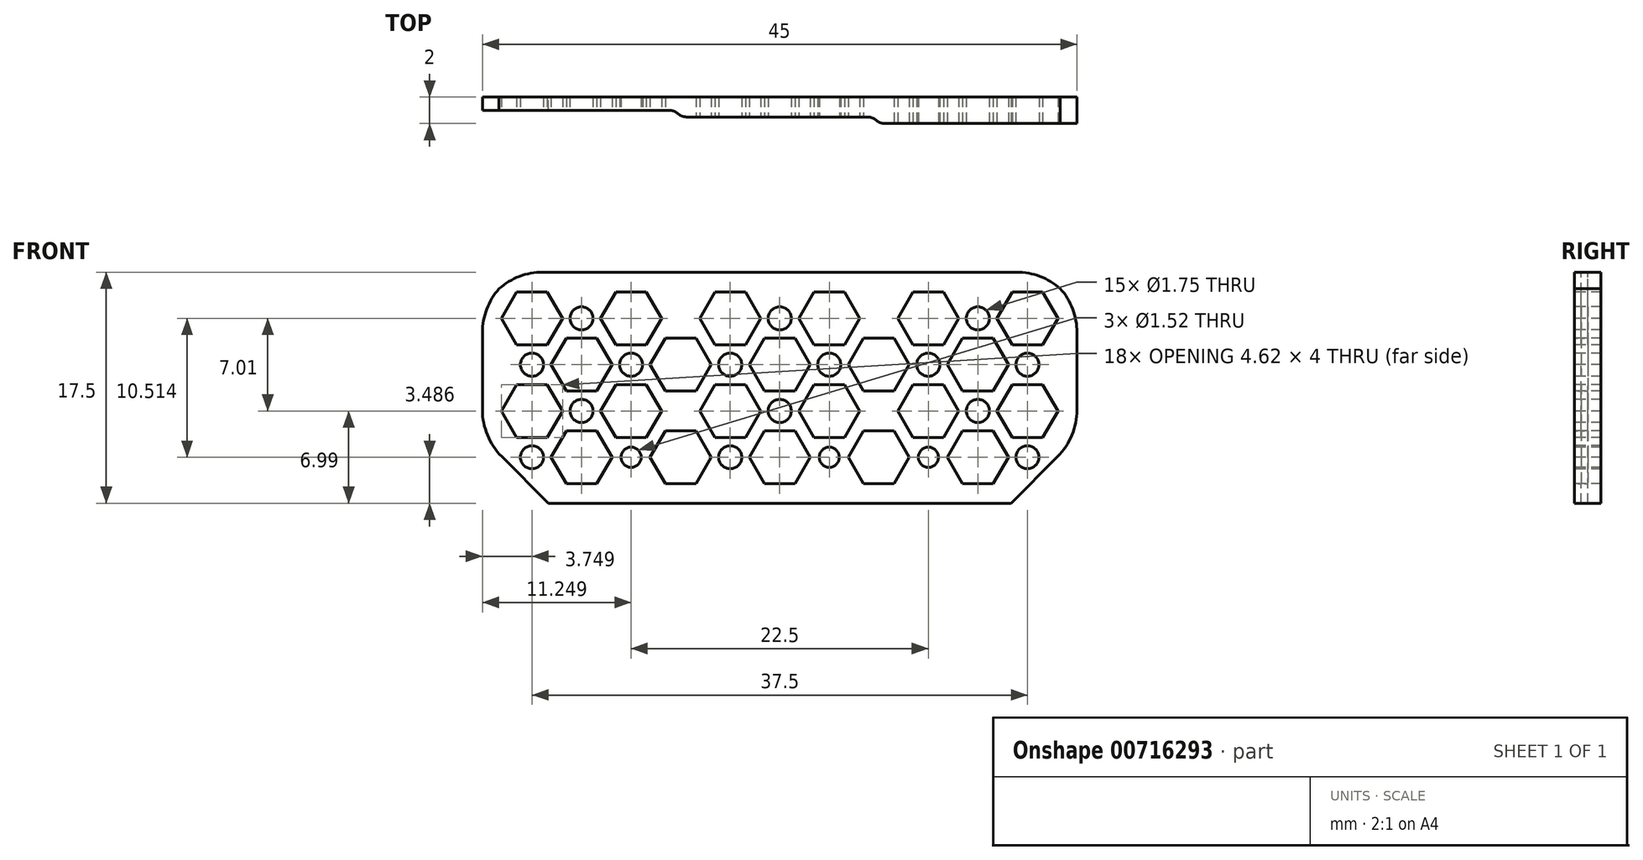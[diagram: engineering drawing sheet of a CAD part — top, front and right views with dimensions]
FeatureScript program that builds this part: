
annotation { "Feature Type Name" : "Feature", "Feature Type Description" : "" }
export const myFeature = defineFeature(function(context is Context, id is Id, definition is map)
    precondition{}
    {
        {
            var Q0;
            Q0=qCreatedBy(makeId("Top.planeOp"),FACE);
            var sketch = newSketch(context, id + "F0", { "sketchPlane" : qUnion([Q0])});
            skLineSegment(sketch, "E0.bottom", {"start": v(-22.5, 0) * mm, "end": v(-7.5, 0) * mm});
            skLineSegment(sketch, "E0.top", {"start": v(-22.5, -1) * mm, "end": v(-7.5, -1) * mm});
            skLineSegment(sketch, "E0.left", {"start": v(-22.5, 0) * mm, "end": v(-22.5, -1) * mm});
            skLineSegment(sketch, "E0.right", {"start": v(-7.5, 0) * mm, "end": v(-7.5, -1) * mm});
            skLineSegment(sketch, "E1.bottom", {"start": v(-7.5, 0) * mm, "end": v(7.5, 0) * mm});
            skLineSegment(sketch, "E1.top", {"start": v(-7.5, -1.5) * mm, "end": v(7.5, -1.5) * mm});
            skLineSegment(sketch, "E1.left", {"start": v(-7.5, 0) * mm, "end": v(-7.5, -1.5) * mm});
            skLineSegment(sketch, "E1.right", {"start": v(7.5, 0) * mm, "end": v(7.5, -1.5) * mm});
            skLineSegment(sketch, "E2.bottom", {"start": v(7.5, 0) * mm, "end": v(22.5, 0) * mm});
            skLineSegment(sketch, "E2.top", {"start": v(7.5, -2) * mm, "end": v(22.5, -2) * mm});
            skLineSegment(sketch, "E2.left", {"start": v(7.5, 0) * mm, "end": v(7.5, -2) * mm});
            skLineSegment(sketch, "E2.right", {"start": v(22.5, 0) * mm, "end": v(22.5, -2) * mm});
            skPoint(sketch, "E3", {"position": v(0, 0) * mm});
            skSolve(sketch);
        }
        {
            var Q0;
            {var subQ0=sQuery(id+"F0.wireOp",EDGE,"E0.bottom");Q0=makeQuery(id+"F0.imprint","IMPRINT",FACE,{"disambiguationData":[TD([[makeQuery(id+"F0.imprint","IMPRINT",EDGE,{"derivedFrom":subQ0}),-1.0]])]});}
            var Q1;
            {var subQ3=sQuery(id+"F0.wireOp",EDGE,"E1.bottom");Q1=makeQuery(id+"F0.imprint","IMPRINT",FACE,{"disambiguationData":[TD([[makeQuery(id+"F0.imprint","IMPRINT",EDGE,{"derivedFrom":subQ3}),-1.0]])]});}
            var Q2;
            {var subQ3=sQuery(id+"F0.wireOp",EDGE,"E2.bottom");Q2=makeQuery(id+"F0.imprint","IMPRINT",FACE,{"disambiguationData":[TD([[makeQuery(id+"F0.imprint","IMPRINT",EDGE,{"derivedFrom":subQ3}),-1.0]])]});}
            extrude(context, id + "F1", {"entities" : qUnion([Q0, Q1, Q2]), "depth" : 17.5 * mm, "offsetDistance" : 25 * mm});
        }
        {
            var Q0;
            Q0=makeQuery(id+"F1.opExtrude","SWEPT_FACE",FACE,{"disambiguationData":[OSD([sQuery(id+"F0.wireOp",EDGE,"E2.top")])]});
            var sketch = newSketch(context, id + "F2", { "sketchPlane" : qUnion([Q0])});
            skLineSegment(sketch, "E4.0.0", {"start": v(-22.5, 0) * mm, "end": v(-7.5, 0) * mm});
            skLineSegment(sketch, "E4.0.1", {"start": v(-7.5, 0) * mm, "end": v(-7.5, 17.5) * mm});
            skLineSegment(sketch, "E4.0.2", {"start": v(-7.5, 17.5) * mm, "end": v(-22.5, 17.5) * mm});
            skLineSegment(sketch, "E4.0.3", {"start": v(-22.5, 17.5) * mm, "end": v(-22.5, 0) * mm});
            skLineSegment(sketch, "E5.0.0", {"start": v(-7.5, 0) * mm, "end": v(7.5, 0) * mm});
            skLineSegment(sketch, "E5.0.1", {"start": v(7.5, 0) * mm, "end": v(7.5, 17.5) * mm});
            skLineSegment(sketch, "E5.0.2", {"start": v(7.5, 17.5) * mm, "end": v(-7.5, 17.5) * mm});
            skLineSegment(sketch, "E5.0.3", {"start": v(-7.5, 17.5) * mm, "end": v(-7.5, 0) * mm});
            skLineSegment(sketch, "E6.0.0", {"start": v(7.5, 0) * mm, "end": v(22.5, 0) * mm});
            skLineSegment(sketch, "E6.0.1", {"start": v(22.5, 0) * mm, "end": v(22.5, 17.5) * mm});
            skLineSegment(sketch, "E6.0.2", {"start": v(22.5, 17.5) * mm, "end": v(7.5, 17.5) * mm});
            skLineSegment(sketch, "E6.0.3", {"start": v(7.5, 17.5) * mm, "end": v(7.5, 0) * mm});
            skCircle(sketch, "E7.cCircle", {"center": v(18.75, 14) * mm, "radius": 2 * mm, "construction": true});
            skLineSegment(sketch, "E7.0", {"start": v(17.6, 12) * mm, "end": v(16.44, 14) * mm});
            skLineSegment(sketch, "E7.1", {"start": v(16.44, 14) * mm, "end": v(17.6, 16) * mm});
            skLineSegment(sketch, "E7.2", {"start": v(17.6, 16) * mm, "end": v(19.9, 16) * mm});
            skLineSegment(sketch, "E7.3", {"start": v(19.9, 16) * mm, "end": v(21.06, 14) * mm});
            skLineSegment(sketch, "E7.4", {"start": v(21.06, 14) * mm, "end": v(19.9, 12) * mm});
            skLineSegment(sketch, "E7.5", {"start": v(19.9, 12) * mm, "end": v(17.6, 12) * mm});
            skPoint(sketch, "E7.0.midPoint", {"position": v(17.02, 13) * mm});
            skPoint(sketch, "E8.1.0.0", {"position": v(9.52, 13) * mm});
            skLineSegment(sketch, "E8.1.0.1", {"start": v(12.4, 12) * mm, "end": v(10.1, 12) * mm});
            skLineSegment(sketch, "E8.1.0.2", {"start": v(12.4, 16) * mm, "end": v(13.56, 14) * mm});
            skCircle(sketch, "E8.1.0.3", {"center": v(11.25, 14) * mm, "radius": 2 * mm, "construction": true});
            skLineSegment(sketch, "E8.1.0.4", {"start": v(13.56, 14) * mm, "end": v(12.4, 12) * mm});
            skLineSegment(sketch, "E8.1.0.5", {"start": v(8.94, 14) * mm, "end": v(10.1, 16) * mm});
            skLineSegment(sketch, "E8.1.0.6", {"start": v(10.1, 16) * mm, "end": v(12.4, 16) * mm});
            skLineSegment(sketch, "E8.1.0.7", {"start": v(10.1, 12) * mm, "end": v(8.94, 14) * mm});
            skPoint(sketch, "E8.2.0.0", {"position": v(2.02, 13) * mm});
            skLineSegment(sketch, "E8.2.0.1", {"start": v(4.9, 12) * mm, "end": v(2.6, 12) * mm});
            skLineSegment(sketch, "E8.2.0.2", {"start": v(4.9, 16) * mm, "end": v(6.06, 14) * mm});
            skCircle(sketch, "E8.2.0.3", {"center": v(3.75, 14) * mm, "radius": 2 * mm, "construction": true});
            skLineSegment(sketch, "E8.2.0.4", {"start": v(6.06, 14) * mm, "end": v(4.9, 12) * mm});
            skLineSegment(sketch, "E8.2.0.5", {"start": v(1.44, 14) * mm, "end": v(2.6, 16) * mm});
            skLineSegment(sketch, "E8.2.0.6", {"start": v(2.6, 16) * mm, "end": v(4.9, 16) * mm});
            skLineSegment(sketch, "E8.2.0.7", {"start": v(2.6, 12) * mm, "end": v(1.44, 14) * mm});
            skLineSegment(sketch, "E8.direction1", {"start": v(17.6, 12) * mm, "end": v(10.1, 12) * mm, "construction": true});
            skPoint(sketch, "E9.0.3.0", {"position": v(-5.48, 13) * mm});
            skLineSegment(sketch, "E9.1.3.0", {"start": v(-2.6, 12) * mm, "end": v(-4.9, 12) * mm});
            skLineSegment(sketch, "E9.4.3.0", {"start": v(-2.6, 16) * mm, "end": v(-1.44, 14) * mm});
            skCircle(sketch, "E9.7.3.0", {"center": v(-3.75, 14) * mm, "radius": 2 * mm, "construction": true});
            skLineSegment(sketch, "E9.9.3.0", {"start": v(-1.44, 14) * mm, "end": v(-2.6, 12) * mm});
            skLineSegment(sketch, "E9.12.3.0", {"start": v(-6.06, 14) * mm, "end": v(-4.9, 16) * mm});
            skLineSegment(sketch, "E9.15.3.0", {"start": v(-4.9, 16) * mm, "end": v(-2.6, 16) * mm});
            skLineSegment(sketch, "E9.18.3.0", {"start": v(-4.9, 12) * mm, "end": v(-6.06, 14) * mm});
            skPoint(sketch, "E9.0.4.0", {"position": v(-12.98, 13) * mm});
            skLineSegment(sketch, "E9.1.4.0", {"start": v(-10.1, 12) * mm, "end": v(-12.4, 12) * mm});
            skLineSegment(sketch, "E9.4.4.0", {"start": v(-10.1, 16) * mm, "end": v(-8.94, 14) * mm});
            skCircle(sketch, "E9.7.4.0", {"center": v(-11.25, 14) * mm, "radius": 2 * mm, "construction": true});
            skLineSegment(sketch, "E9.9.4.0", {"start": v(-8.94, 14) * mm, "end": v(-10.1, 12) * mm});
            skLineSegment(sketch, "E9.12.4.0", {"start": v(-13.56, 14) * mm, "end": v(-12.4, 16) * mm});
            skLineSegment(sketch, "E9.15.4.0", {"start": v(-12.4, 16) * mm, "end": v(-10.1, 16) * mm});
            skLineSegment(sketch, "E9.18.4.0", {"start": v(-12.4, 12) * mm, "end": v(-13.56, 14) * mm});
            skPoint(sketch, "E9.0.5.0", {"position": v(-20.48, 13) * mm});
            skLineSegment(sketch, "E9.1.5.0", {"start": v(-17.6, 12) * mm, "end": v(-19.9, 12) * mm});
            skLineSegment(sketch, "E9.4.5.0", {"start": v(-17.6, 16) * mm, "end": v(-16.44, 14) * mm});
            skCircle(sketch, "E9.7.5.0", {"center": v(-18.75, 14) * mm, "radius": 2 * mm, "construction": true});
            skLineSegment(sketch, "E9.9.5.0", {"start": v(-16.44, 14) * mm, "end": v(-17.6, 12) * mm});
            skLineSegment(sketch, "E9.12.5.0", {"start": v(-21.06, 14) * mm, "end": v(-19.9, 16) * mm});
            skLineSegment(sketch, "E9.15.5.0", {"start": v(-19.9, 16) * mm, "end": v(-17.6, 16) * mm});
            skLineSegment(sketch, "E9.18.5.0", {"start": v(-19.9, 12) * mm, "end": v(-21.06, 14) * mm});
            skCircle(sketch, "E10.cCircle", {"center": v(15, 10.5) * mm, "radius": 2 * mm, "construction": true});
            skLineSegment(sketch, "E10.0", {"start": v(12.69, 10.5) * mm, "end": v(13.84, 12.5) * mm});
            skLineSegment(sketch, "E10.1", {"start": v(13.84, 12.5) * mm, "end": v(16.15, 12.5) * mm});
            skLineSegment(sketch, "E10.2", {"start": v(16.15, 12.5) * mm, "end": v(17.3, 10.5) * mm});
            skLineSegment(sketch, "E10.3", {"start": v(17.3, 10.5) * mm, "end": v(16.15, 8.5) * mm});
            skLineSegment(sketch, "E10.4", {"start": v(16.15, 8.5) * mm, "end": v(13.84, 8.5) * mm});
            skLineSegment(sketch, "E10.5", {"start": v(13.84, 8.5) * mm, "end": v(12.69, 10.5) * mm});
            skPoint(sketch, "E10.0.midPoint", {"position": v(13.27, 11.5) * mm});
            skLineSegment(sketch, "E11.1.0.1", {"start": v(10.1, 12) * mm, "end": v(2.6, 12) * mm, "construction": true});
            skLineSegment(sketch, "E11.1.0.2", {"start": v(6.34, 12.5) * mm, "end": v(8.65, 12.5) * mm});
            skPoint(sketch, "E11.1.0.3", {"position": v(5.77, 11.5) * mm});
            skCircle(sketch, "E11.1.0.4", {"center": v(7.5, 10.5) * mm, "radius": 2 * mm, "construction": true});
            skLineSegment(sketch, "E11.1.0.5", {"start": v(5.19, 10.5) * mm, "end": v(6.34, 12.5) * mm});
            skLineSegment(sketch, "E11.1.0.6", {"start": v(8.65, 8.5) * mm, "end": v(6.34, 8.5) * mm});
            skLineSegment(sketch, "E11.1.0.7", {"start": v(8.65, 12.5) * mm, "end": v(9.8, 10.5) * mm});
            skLineSegment(sketch, "E11.1.0.8", {"start": v(6.34, 8.5) * mm, "end": v(5.19, 10.5) * mm});
            skLineSegment(sketch, "E11.1.0.9", {"start": v(9.8, 10.5) * mm, "end": v(8.65, 8.5) * mm});
            skLineSegment(sketch, "E11.2.0.1", {"start": v(2.6, 12) * mm, "end": v(-4.9, 12) * mm, "construction": true});
            skLineSegment(sketch, "E11.2.0.2", {"start": v(-1.16, 12.5) * mm, "end": v(1.15, 12.5) * mm});
            skPoint(sketch, "E11.2.0.3", {"position": v(-1.73, 11.5) * mm});
            skCircle(sketch, "E11.2.0.4", {"center": v(0, 10.5) * mm, "radius": 2 * mm, "construction": true});
            skLineSegment(sketch, "E11.2.0.5", {"start": v(-2.31, 10.5) * mm, "end": v(-1.16, 12.5) * mm});
            skLineSegment(sketch, "E11.2.0.6", {"start": v(1.15, 8.5) * mm, "end": v(-1.16, 8.5) * mm});
            skLineSegment(sketch, "E11.2.0.7", {"start": v(1.15, 12.5) * mm, "end": v(2.3, 10.5) * mm});
            skLineSegment(sketch, "E11.2.0.8", {"start": v(-1.16, 8.5) * mm, "end": v(-2.31, 10.5) * mm});
            skLineSegment(sketch, "E11.2.0.9", {"start": v(2.3, 10.5) * mm, "end": v(1.15, 8.5) * mm});
            skLineSegment(sketch, "E11.3.0.1", {"start": v(-4.9, 12) * mm, "end": v(-12.4, 12) * mm, "construction": true});
            skLineSegment(sketch, "E11.3.0.2", {"start": v(-8.66, 12.5) * mm, "end": v(-6.35, 12.5) * mm});
            skPoint(sketch, "E11.3.0.3", {"position": v(-9.23, 11.5) * mm});
            skCircle(sketch, "E11.3.0.4", {"center": v(-7.5, 10.5) * mm, "radius": 2 * mm, "construction": true});
            skLineSegment(sketch, "E11.3.0.5", {"start": v(-9.81, 10.5) * mm, "end": v(-8.66, 12.5) * mm});
            skLineSegment(sketch, "E11.3.0.6", {"start": v(-6.35, 8.5) * mm, "end": v(-8.66, 8.5) * mm});
            skLineSegment(sketch, "E11.3.0.7", {"start": v(-6.35, 12.5) * mm, "end": v(-5.2, 10.5) * mm});
            skLineSegment(sketch, "E11.3.0.8", {"start": v(-8.66, 8.5) * mm, "end": v(-9.8, 10.5) * mm});
            skLineSegment(sketch, "E11.3.0.9", {"start": v(-5.2, 10.5) * mm, "end": v(-6.35, 8.5) * mm});
            skLineSegment(sketch, "E11.4.0.1", {"start": v(-12.4, 12) * mm, "end": v(-19.9, 12) * mm, "construction": true});
            skLineSegment(sketch, "E11.4.0.2", {"start": v(-16.16, 12.5) * mm, "end": v(-13.85, 12.5) * mm});
            skPoint(sketch, "E11.4.0.3", {"position": v(-16.73, 11.5) * mm});
            skCircle(sketch, "E11.4.0.4", {"center": v(-15, 10.5) * mm, "radius": 2 * mm, "construction": true});
            skLineSegment(sketch, "E11.4.0.5", {"start": v(-17.31, 10.5) * mm, "end": v(-16.16, 12.5) * mm});
            skLineSegment(sketch, "E11.4.0.6", {"start": v(-13.85, 8.5) * mm, "end": v(-16.16, 8.5) * mm});
            skLineSegment(sketch, "E11.4.0.7", {"start": v(-13.85, 12.5) * mm, "end": v(-12.7, 10.5) * mm});
            skLineSegment(sketch, "E11.4.0.8", {"start": v(-16.16, 8.5) * mm, "end": v(-17.3, 10.5) * mm});
            skLineSegment(sketch, "E11.4.0.9", {"start": v(-12.7, 10.5) * mm, "end": v(-13.85, 8.5) * mm});
            skLineSegment(sketch, "E11.direction1", {"start": v(10.1, 12) * mm, "end": v(2.6, 12) * mm, "construction": true});
            skPoint(sketch, "E12.1.0.0", {"position": v(-5.48, 6) * mm});
            skLineSegment(sketch, "E12.1.0.1", {"start": v(2.6, 9) * mm, "end": v(4.9, 9) * mm});
            skPoint(sketch, "E12.1.0.2", {"position": v(-20.48, 6) * mm});
            skLineSegment(sketch, "E12.1.0.3", {"start": v(-12.4, 9) * mm, "end": v(-10.1, 9) * mm});
            skLineSegment(sketch, "E12.1.0.4", {"start": v(-17.6, 9) * mm, "end": v(-16.44, 7) * mm});
            skPoint(sketch, "E12.1.0.5", {"position": v(9.52, 6) * mm});
            skPoint(sketch, "E12.1.0.6", {"position": v(2.02, 6) * mm});
            skPoint(sketch, "E12.1.0.7", {"position": v(17.02, 6) * mm});
            skLineSegment(sketch, "E12.1.0.8", {"start": v(1.44, 7) * mm, "end": v(2.6, 9) * mm});
            skLineSegment(sketch, "E12.1.0.9", {"start": v(-10.1, 9) * mm, "end": v(-8.94, 7) * mm});
            skLineSegment(sketch, "E12.1.0.10", {"start": v(-2.6, 9) * mm, "end": v(-1.44, 7) * mm});
            skPoint(sketch, "E12.1.0.11", {"position": v(-12.98, 6) * mm});
            skLineSegment(sketch, "E12.1.0.12", {"start": v(19.9, 9) * mm, "end": v(21.06, 7) * mm});
            skLineSegment(sketch, "E12.1.0.13", {"start": v(17.6, 9) * mm, "end": v(19.9, 9) * mm});
            skLineSegment(sketch, "E12.1.0.14", {"start": v(16.44, 7) * mm, "end": v(17.6, 9) * mm});
            skLineSegment(sketch, "E12.1.0.15", {"start": v(10.1, 9) * mm, "end": v(12.4, 9) * mm});
            skLineSegment(sketch, "E12.1.0.16", {"start": v(8.94, 7) * mm, "end": v(10.1, 9) * mm});
            skLineSegment(sketch, "E12.1.0.17", {"start": v(-4.9, 9) * mm, "end": v(-2.6, 9) * mm});
            skLineSegment(sketch, "E12.1.0.18", {"start": v(-13.56, 7) * mm, "end": v(-12.4, 9) * mm});
            skLineSegment(sketch, "E12.1.0.19", {"start": v(-6.06, 7) * mm, "end": v(-4.9, 9) * mm});
            skLineSegment(sketch, "E12.1.0.20", {"start": v(-19.9, 9) * mm, "end": v(-17.6, 9) * mm});
            skLineSegment(sketch, "E12.1.0.21", {"start": v(-21.06, 7) * mm, "end": v(-19.9, 9) * mm});
            skLineSegment(sketch, "E12.1.0.22", {"start": v(12.4, 9) * mm, "end": v(13.56, 7) * mm});
            skLineSegment(sketch, "E12.1.0.23", {"start": v(4.9, 9) * mm, "end": v(6.06, 7) * mm});
            skPoint(sketch, "E12.1.0.24", {"position": v(-12.98, 6) * mm});
            skPoint(sketch, "E12.1.0.25", {"position": v(2.02, 6) * mm});
            skPoint(sketch, "E12.1.0.26", {"position": v(-5.48, 6) * mm});
            skPoint(sketch, "E12.1.0.27", {"position": v(9.52, 6) * mm});
            skLineSegment(sketch, "E12.1.0.28", {"start": v(21.06, 7) * mm, "end": v(19.9, 5) * mm});
            skCircle(sketch, "E12.1.0.29", {"center": v(18.75, 7) * mm, "radius": 2 * mm, "construction": true});
            skLineSegment(sketch, "E12.1.0.30", {"start": v(17.6, 5) * mm, "end": v(16.44, 7) * mm});
            skLineSegment(sketch, "E12.1.0.31", {"start": v(19.9, 5) * mm, "end": v(17.6, 5) * mm});
            skLineSegment(sketch, "E12.1.0.32", {"start": v(17.6, 5) * mm, "end": v(10.1, 5) * mm, "construction": true});
            skLineSegment(sketch, "E12.1.0.33", {"start": v(10.1, 5) * mm, "end": v(8.94, 7) * mm});
            skLineSegment(sketch, "E12.1.0.34", {"start": v(10.1, 5) * mm, "end": v(2.6, 5) * mm, "construction": true});
            skLineSegment(sketch, "E12.1.0.35", {"start": v(13.56, 7) * mm, "end": v(12.4, 5) * mm});
            skCircle(sketch, "E12.1.0.36", {"center": v(11.25, 7) * mm, "radius": 2 * mm, "construction": true});
            skLineSegment(sketch, "E12.1.0.37", {"start": v(10.1, 5) * mm, "end": v(2.6, 5) * mm, "construction": true});
            skLineSegment(sketch, "E12.1.0.38", {"start": v(12.4, 5) * mm, "end": v(10.1, 5) * mm});
            skCircle(sketch, "E12.1.0.39", {"center": v(3.75, 7) * mm, "radius": 2 * mm, "construction": true});
            skLineSegment(sketch, "E12.1.0.40", {"start": v(4.9, 5) * mm, "end": v(2.6, 5) * mm});
            skLineSegment(sketch, "E12.1.0.41", {"start": v(2.6, 5) * mm, "end": v(1.44, 7) * mm});
            skLineSegment(sketch, "E12.1.0.42", {"start": v(2.6, 5) * mm, "end": v(-4.9, 5) * mm, "construction": true});
            skLineSegment(sketch, "E12.1.0.43", {"start": v(6.06, 7) * mm, "end": v(4.9, 5) * mm});
            skLineSegment(sketch, "E12.1.0.44", {"start": v(-4.9, 5) * mm, "end": v(-12.4, 5) * mm, "construction": true});
            skLineSegment(sketch, "E12.1.0.45", {"start": v(-4.9, 5) * mm, "end": v(-6.06, 7) * mm});
            skLineSegment(sketch, "E12.1.0.46", {"start": v(-1.44, 7) * mm, "end": v(-2.6, 5) * mm});
            skCircle(sketch, "E12.1.0.47", {"center": v(-3.75, 7) * mm, "radius": 2 * mm, "construction": true});
            skLineSegment(sketch, "E12.1.0.48", {"start": v(-2.6, 5) * mm, "end": v(-4.9, 5) * mm});
            skLineSegment(sketch, "E12.1.0.49", {"start": v(-12.4, 5) * mm, "end": v(-13.56, 7) * mm});
            skLineSegment(sketch, "E12.1.0.50", {"start": v(-8.94, 7) * mm, "end": v(-10.1, 5) * mm});
            skLineSegment(sketch, "E12.1.0.51", {"start": v(-12.4, 5) * mm, "end": v(-19.9, 5) * mm, "construction": true});
            skCircle(sketch, "E12.1.0.52", {"center": v(-11.25, 7) * mm, "radius": 2 * mm, "construction": true});
            skLineSegment(sketch, "E12.1.0.53", {"start": v(-10.1, 5) * mm, "end": v(-12.4, 5) * mm});
            skCircle(sketch, "E12.1.0.54", {"center": v(-18.75, 7) * mm, "radius": 2 * mm, "construction": true});
            skLineSegment(sketch, "E12.1.0.55", {"start": v(-16.44, 7) * mm, "end": v(-17.6, 5) * mm});
            skLineSegment(sketch, "E12.1.0.56", {"start": v(-19.9, 5) * mm, "end": v(-21.06, 7) * mm});
            skLineSegment(sketch, "E12.1.0.57", {"start": v(-17.6, 5) * mm, "end": v(-19.9, 5) * mm});
            skLineSegment(sketch, "E12.direction1", {"start": v(-20.48, 13) * mm, "end": v(-20.48, 6) * mm, "construction": true});
            skLineSegment(sketch, "E13.1.0.1", {"start": v(16.15, 1.49) * mm, "end": v(13.84, 1.49) * mm});
            skPoint(sketch, "E13.1.0.2", {"position": v(13.27, 4.49) * mm});
            skCircle(sketch, "E13.1.0.4", {"center": v(15, 3.49) * mm, "radius": 2 * mm, "construction": true});
            skLineSegment(sketch, "E13.1.0.5", {"start": v(13.84, 1.49) * mm, "end": v(12.69, 3.49) * mm});
            skLineSegment(sketch, "E13.1.0.6", {"start": v(17.3, 3.49) * mm, "end": v(16.15, 1.49) * mm});
            skLineSegment(sketch, "E13.1.0.7", {"start": v(16.15, 5.49) * mm, "end": v(17.3, 3.49) * mm});
            skLineSegment(sketch, "E13.1.0.8", {"start": v(13.84, 5.49) * mm, "end": v(16.15, 5.49) * mm});
            skLineSegment(sketch, "E13.1.0.9", {"start": v(12.69, 3.49) * mm, "end": v(13.84, 5.49) * mm});
            skPoint(sketch, "E13.1.0.10", {"position": v(5.77, 4.49) * mm});
            skLineSegment(sketch, "E13.1.0.11", {"start": v(9.8, 3.49) * mm, "end": v(8.65, 1.49) * mm});
            skCircle(sketch, "E13.1.0.12", {"center": v(7.5, 3.49) * mm, "radius": 2 * mm, "construction": true});
            skLineSegment(sketch, "E13.1.0.13", {"start": v(6.34, 5.49) * mm, "end": v(8.65, 5.49) * mm});
            skLineSegment(sketch, "E13.1.0.16", {"start": v(8.65, 1.49) * mm, "end": v(6.34, 1.49) * mm});
            skLineSegment(sketch, "E13.1.0.17", {"start": v(7.5, 10.5) * mm, "end": v(7.5, -7) * mm});
            skLineSegment(sketch, "E13.1.0.19", {"start": v(8.65, 5.49) * mm, "end": v(9.8, 3.49) * mm});
            skLineSegment(sketch, "E13.1.0.21", {"start": v(6.34, 1.49) * mm, "end": v(5.19, 3.49) * mm});
            skLineSegment(sketch, "E13.1.0.22", {"start": v(7.5, -7) * mm, "end": v(7.5, 10.5) * mm});
            skLineSegment(sketch, "E13.1.0.23", {"start": v(5.19, 3.49) * mm, "end": v(6.34, 5.49) * mm});
            skLineSegment(sketch, "E13.1.0.24", {"start": v(-1.16, 1.49) * mm, "end": v(-2.31, 3.49) * mm});
            skPoint(sketch, "E13.1.0.26", {"position": v(-1.73, 4.49) * mm});
            skCircle(sketch, "E13.1.0.27", {"center": v(0, 3.49) * mm, "radius": 2 * mm, "construction": true});
            skLineSegment(sketch, "E13.1.0.28", {"start": v(2.3, 3.49) * mm, "end": v(1.15, 1.49) * mm});
            skLineSegment(sketch, "E13.1.0.29", {"start": v(1.15, 1.49) * mm, "end": v(-1.16, 1.49) * mm});
            skLineSegment(sketch, "E13.1.0.30", {"start": v(-2.31, 3.49) * mm, "end": v(-1.16, 5.49) * mm});
            skLineSegment(sketch, "E13.1.0.31", {"start": v(1.15, 5.49) * mm, "end": v(2.3, 3.49) * mm});
            skLineSegment(sketch, "E13.1.0.32", {"start": v(-5.2, 3.49) * mm, "end": v(-6.35, 1.49) * mm});
            skCircle(sketch, "E13.1.0.33", {"center": v(-7.5, 3.49) * mm, "radius": 2 * mm, "construction": true});
            skPoint(sketch, "E13.1.0.35", {"position": v(-9.23, 4.49) * mm});
            skLineSegment(sketch, "E13.1.0.37", {"start": v(-8.66, 1.49) * mm, "end": v(-9.81, 3.49) * mm});
            skLineSegment(sketch, "E13.1.0.38", {"start": v(-7.5, 10.5) * mm, "end": v(-7.5, -7) * mm});
            skLineSegment(sketch, "E13.1.0.39", {"start": v(-6.35, 5.49) * mm, "end": v(-5.2, 3.49) * mm});
            skLineSegment(sketch, "E13.1.0.40", {"start": v(-8.66, 5.49) * mm, "end": v(-6.35, 5.49) * mm});
            skLineSegment(sketch, "E13.1.0.41", {"start": v(-6.35, 1.49) * mm, "end": v(-8.66, 1.49) * mm});
            skLineSegment(sketch, "E13.1.0.43", {"start": v(-7.5, -7) * mm, "end": v(-7.5, 10.5) * mm});
            skLineSegment(sketch, "E13.1.0.44", {"start": v(-9.81, 3.49) * mm, "end": v(-8.66, 5.49) * mm});
            skLineSegment(sketch, "E13.1.0.45", {"start": v(-1.16, 5.49) * mm, "end": v(1.15, 5.49) * mm});
            skLineSegment(sketch, "E13.1.0.46", {"start": v(-13.85, 1.49) * mm, "end": v(-16.16, 1.49) * mm});
            skPoint(sketch, "E13.1.0.47", {"position": v(-16.73, 4.49) * mm});
            skCircle(sketch, "E13.1.0.50", {"center": v(-15, 3.49) * mm, "radius": 2 * mm, "construction": true});
            skLineSegment(sketch, "E13.1.0.52", {"start": v(-16.16, 1.49) * mm, "end": v(-17.3, 3.49) * mm});
            skLineSegment(sketch, "E13.1.0.53", {"start": v(-17.31, 3.49) * mm, "end": v(-16.16, 5.49) * mm});
            skLineSegment(sketch, "E13.1.0.54", {"start": v(-16.16, 5.49) * mm, "end": v(-13.85, 5.49) * mm});
            skLineSegment(sketch, "E13.1.0.55", {"start": v(-12.7, 3.49) * mm, "end": v(-13.85, 1.49) * mm});
            skLineSegment(sketch, "E13.1.0.56", {"start": v(-13.85, 5.49) * mm, "end": v(-12.7, 3.49) * mm});
            skLineSegment(sketch, "E13.direction1", {"start": v(-7.5, 0) * mm, "end": v(-7.5, -7) * mm, "construction": true});
            skLineSegment(sketch, "E14", {"start": v(-18.75, 7) * mm, "end": v(18.75, 7) * mm, "construction": true});
            skLineSegment(sketch, "E15", {"start": v(-15, 10.5) * mm, "end": v(-15, 3.49) * mm, "construction": true});
            skLineSegment(sketch, "E16", {"start": v(-18.75, 14) * mm, "end": v(-11.25, 14) * mm, "construction": true});
            skLineSegment(sketch, "E17", {"start": v(-15, 10.5) * mm, "end": v(-15, 14) * mm, "construction": true});
            skLineSegment(sketch, "E18", {"start": v(-15, 14) * mm, "end": v(18.75, 14) * mm, "construction": true});
            skLineSegment(sketch, "E19", {"start": v(-11.25, 14) * mm, "end": v(-11.25, 7) * mm, "construction": true});
            skLineSegment(sketch, "E20", {"start": v(-7.5, 10.5) * mm, "end": v(-7.5, 3.49) * mm, "construction": true});
            skLineSegment(sketch, "E21", {"start": v(-15, 3.49) * mm, "end": v(15, 3.49) * mm, "construction": true});
            skLineSegment(sketch, "E22", {"start": v(15, 10.5) * mm, "end": v(-15, 10.5) * mm, "construction": true});
            skLineSegment(sketch, "E23", {"start": v(-3.75, 14) * mm, "end": v(-3.75, 7) * mm, "construction": true});
            skLineSegment(sketch, "E24", {"start": v(0, 10.5) * mm, "end": v(0, 3.49) * mm, "construction": true});
            skCircle(sketch, "E25", {"center": v(-15, 7) * mm, "radius": 0.88 * mm});
            skCircle(sketch, "E26", {"center": v(-15, 14) * mm, "radius": 0.88 * mm});
            skLineSegment(sketch, "E27", {"start": v(-11.25, 7) * mm, "end": v(-11.25, -10.08) * mm, "construction": true});
            skLineSegment(sketch, "E28", {"start": v(-3.75, 14) * mm, "end": v(-3.75, -4.1) * mm, "construction": true});
            skLineSegment(sketch, "E29", {"start": v(3.75, 14) * mm, "end": v(3.75, -3.7) * mm, "construction": true});
            skLineSegment(sketch, "E30", {"start": v(11.25, 14) * mm, "end": v(11.25, -4.55) * mm, "construction": true});
            skLineSegment(sketch, "E31", {"start": v(18.75, 14) * mm, "end": v(18.75, -4.4) * mm, "construction": true});
            skLineSegment(sketch, "E32", {"start": v(15, 3.49) * mm, "end": v(18.75, 3.49) * mm, "construction": true});
            skLineSegment(sketch, "E33", {"start": v(15, 10.5) * mm, "end": v(18.75, 10.5) * mm, "construction": true});
            skCircle(sketch, "E34", {"center": v(-7.5, 14) * mm, "radius": 0.88 * mm});
            skCircle(sketch, "E35", {"center": v(-7.5, 6.99) * mm, "radius": 0.88 * mm});
            skCircle(sketch, "E36", {"center": v(0, 7) * mm, "radius": 0.88 * mm});
            skCircle(sketch, "E37", {"center": v(0, 14) * mm, "radius": 0.88 * mm});
            skPoint(sketch, "E37.centerSnap0", {"position": v(0, 12.5) * mm});
            skCircle(sketch, "E38", {"center": v(7.5, 14) * mm, "radius": 0.88 * mm});
            skCircle(sketch, "E39", {"center": v(7.5, 7) * mm, "radius": 0.88 * mm});
            skCircle(sketch, "E40", {"center": v(15, 7) * mm, "radius": 0.88 * mm});
            skPoint(sketch, "E40.centerSnap0", {"position": v(15, 5.49) * mm});
            skCircle(sketch, "E41", {"center": v(15, 14) * mm, "radius": 0.88 * mm});
            skPoint(sketch, "E41.centerSnap0", {"position": v(15, 12.5) * mm});
            skCircle(sketch, "E42", {"center": v(18.75, 3.49) * mm, "radius": 0.88 * mm});
            skCircle(sketch, "E43", {"center": v(11.25, 3.49) * mm, "radius": 0.76 * mm});
            skCircle(sketch, "E44", {"center": v(-11.25, 3.49) * mm, "radius": 0.76 * mm});
            skCircle(sketch, "E45", {"center": v(-18.75, 3.49) * mm, "radius": 0.88 * mm});
            skPoint(sketch, "E45.centerSnap0", {"position": v(-18.75, 5) * mm});
            skCircle(sketch, "E46", {"center": v(-18.75, 10.5) * mm, "radius": 0.88 * mm});
            skPoint(sketch, "E46.centerSnap0", {"position": v(-18.75, 12) * mm});
            skCircle(sketch, "E47", {"center": v(-3.75, 3.49) * mm, "radius": 0.88 * mm});
            skCircle(sketch, "E48", {"center": v(3.75, 3.49) * mm, "radius": 0.76 * mm});
            skCircle(sketch, "E49", {"center": v(-3.75, 10.5) * mm, "radius": 0.88 * mm});
            skCircle(sketch, "E50", {"center": v(3.75, 10.5) * mm, "radius": 0.88 * mm});
            skCircle(sketch, "E51", {"center": v(11.25, 10.5) * mm, "radius": 0.88 * mm});
            skCircle(sketch, "E52", {"center": v(18.75, 10.5) * mm, "radius": 0.88 * mm});
            skCircle(sketch, "E53", {"center": v(-11.25, 10.5) * mm, "radius": 0.88 * mm});
            skSolve(sketch);
        }
        {
            var Q0;
            Q0=makeQuery(id+"F2.imprint","IMPRINT",FACE,{"disambiguationData":[TD([[makeQuery(id+"F2.imprint","IMPRINT",EDGE,{"derivedFrom":sQuery(id+"F2.wireOp",EDGE,"E9.1.5.0")}),-1.0]])]});
            var Q1;
            Q1=makeQuery(id+"F2.imprint","IMPRINT",FACE,{"disambiguationData":[TD([[makeQuery(id+"F2.imprint","IMPRINT",EDGE,{"derivedFrom":sQuery(id+"F2.wireOp",EDGE,"E46")}),1.0]])]});
            var Q2;
            Q2=makeQuery(id+"F2.imprint","IMPRINT",FACE,{"disambiguationData":[TD([[makeQuery(id+"F2.imprint","IMPRINT",EDGE,{"derivedFrom":sQuery(id+"F2.wireOp",EDGE,"E12.1.0.4")}),-1.0]])]});
            var Q3;
            Q3=makeQuery(id+"F2.imprint","IMPRINT",FACE,{"disambiguationData":[TD([[makeQuery(id+"F2.imprint","IMPRINT",EDGE,{"derivedFrom":sQuery(id+"F2.wireOp",EDGE,"E45")}),1.0]])]});
            var Q4;
            Q4=makeQuery(id+"F2.imprint","IMPRINT",FACE,{"disambiguationData":[TD([[makeQuery(id+"F2.imprint","IMPRINT",EDGE,{"derivedFrom":sQuery(id+"F2.wireOp",EDGE,"E13.1.0.46")}),-1.0]])]});
            var Q5;
            Q5=makeQuery(id+"F2.imprint","IMPRINT",FACE,{"disambiguationData":[TD([[makeQuery(id+"F2.imprint","IMPRINT",EDGE,{"derivedFrom":sQuery(id+"F2.wireOp",EDGE,"E25")}),1.0]])]});
            var Q6;
            Q6=makeQuery(id+"F2.imprint","IMPRINT",FACE,{"disambiguationData":[TD([[makeQuery(id+"F2.imprint","IMPRINT",EDGE,{"derivedFrom":sQuery(id+"F2.wireOp",EDGE,"E11.4.0.2")}),-1.0]])]});
            var Q7;
            Q7=makeQuery(id+"F2.imprint","IMPRINT",FACE,{"disambiguationData":[TD([[makeQuery(id+"F2.imprint","IMPRINT",EDGE,{"derivedFrom":sQuery(id+"F2.wireOp",EDGE,"E26")}),1.0]])]});
            var Q8;
            Q8=makeQuery(id+"F2.imprint","IMPRINT",FACE,{"disambiguationData":[TD([[makeQuery(id+"F2.imprint","IMPRINT",EDGE,{"derivedFrom":sQuery(id+"F2.wireOp",EDGE,"E9.1.4.0")}),-1.0]])]});
            var Q9;
            Q9=makeQuery(id+"F2.imprint","IMPRINT",FACE,{"disambiguationData":[TD([[makeQuery(id+"F2.imprint","IMPRINT",EDGE,{"derivedFrom":sQuery(id+"F2.wireOp",EDGE,"E12.1.0.3")}),-1.0]])]});
            var Q10;
            Q10=makeQuery(id+"F2.imprint","IMPRINT",FACE,{"disambiguationData":[TD([[makeQuery(id+"F2.imprint","IMPRINT",EDGE,{"derivedFrom":sQuery(id+"F2.wireOp",EDGE,"E44")}),1.0]])]});
            var Q11;
            {var subQ5=sQuery(id+"F2.wireOp",EDGE,"E13.1.0.32");Q11=makeQuery(id+"F2.imprint","IMPRINT",FACE,{"disambiguationData":[TD([[makeQuery(id+"F2.imprint","IMPRINT",EDGE,{"derivedFrom":subQ5}),-1.0]])]});}
            var Q12;
            {var subQ6=sQuery(id+"F2.wireOp",EDGE,"E13.1.0.37");Q12=makeQuery(id+"F2.imprint","IMPRINT",FACE,{"disambiguationData":[TD([[makeQuery(id+"F2.imprint","IMPRINT",EDGE,{"derivedFrom":subQ6}),-1.0]])]});}
            var Q13;
            {var subQ0=sQuery(id+"F2.wireOp",EDGE,"E35");var subQ1=sQuery(id+"F2.wireOp",EDGE,"E13.1.0.43");var subQ2=makeQuery(id+"F2.imprint","INTERSECT",VERTEX,{"disambiguationData":[OD(0.0)],"derivedFrom":[subQ1,subQ0]});Q13=makeQuery(id+"F2.imprint","IMPRINT",FACE,{"disambiguationData":[TD([[makeQuery(id+"F2.imprint","IMPRINT",EDGE,{"disambiguationData":[TD([[subQ2,-1.0]])],"derivedFrom":subQ1}),1.0]])]});}
            var Q14;
            {var subQ0=sQuery(id+"F2.wireOp",EDGE,"E35");var subQ1=sQuery(id+"F2.wireOp",EDGE,"E13.1.0.43");var subQ2=makeQuery(id+"F2.imprint","INTERSECT",VERTEX,{"disambiguationData":[OD(0.0)],"derivedFrom":[subQ1,subQ0]});Q14=makeQuery(id+"F2.imprint","IMPRINT",FACE,{"disambiguationData":[TD([[makeQuery(id+"F2.imprint","IMPRINT",EDGE,{"disambiguationData":[TD([[subQ2,-1.0]])],"derivedFrom":subQ1}),-1.0]])]});}
            var Q15;
            {var subQ0=sQuery(id+"F2.wireOp",EDGE,"E11.3.0.7");Q15=makeQuery(id+"F2.imprint","IMPRINT",FACE,{"disambiguationData":[TD([[makeQuery(id+"F2.imprint","IMPRINT",EDGE,{"derivedFrom":subQ0}),-1.0]])]});}
            var Q16;
            {var subQ4=sQuery(id+"F2.wireOp",EDGE,"E11.3.0.5");Q16=makeQuery(id+"F2.imprint","IMPRINT",FACE,{"disambiguationData":[TD([[makeQuery(id+"F2.imprint","IMPRINT",EDGE,{"derivedFrom":subQ4}),-1.0]])]});}
            var Q17;
            {var subQ0=sQuery(id+"F2.wireOp",EDGE,"E34");var subQ1=sQuery(id+"F2.wireOp",EDGE,"E5.0.3");var subQ2=makeQuery(id+"F2.imprint","INTERSECT",VERTEX,{"disambiguationData":[OD(0.0)],"derivedFrom":[subQ1,subQ0]});Q17=makeQuery(id+"F2.imprint","IMPRINT",FACE,{"disambiguationData":[TD([[makeQuery(id+"F2.imprint","IMPRINT",EDGE,{"disambiguationData":[TD([[subQ2,-1.0]])],"derivedFrom":subQ1}),-1.0]])]});}
            var Q18;
            {var subQ0=sQuery(id+"F2.wireOp",EDGE,"E34");var subQ1=sQuery(id+"F2.wireOp",EDGE,"E5.0.3");var subQ2=makeQuery(id+"F2.imprint","INTERSECT",VERTEX,{"disambiguationData":[OD(0.0)],"derivedFrom":[subQ1,subQ0]});Q18=makeQuery(id+"F2.imprint","IMPRINT",FACE,{"disambiguationData":[TD([[makeQuery(id+"F2.imprint","IMPRINT",EDGE,{"disambiguationData":[TD([[subQ2,-1.0]])],"derivedFrom":subQ1}),1.0]])]});}
            var Q19;
            Q19=makeQuery(id+"F2.imprint","IMPRINT",FACE,{"disambiguationData":[TD([[makeQuery(id+"F2.imprint","IMPRINT",EDGE,{"derivedFrom":sQuery(id+"F2.wireOp",EDGE,"E9.1.3.0")}),-1.0]])]});
            var Q20;
            Q20=makeQuery(id+"F2.imprint","IMPRINT",FACE,{"disambiguationData":[TD([[makeQuery(id+"F2.imprint","IMPRINT",EDGE,{"derivedFrom":sQuery(id+"F2.wireOp",EDGE,"E12.1.0.10")}),-1.0]])]});
            var Q21;
            Q21=makeQuery(id+"F2.imprint","IMPRINT",FACE,{"disambiguationData":[TD([[makeQuery(id+"F2.imprint","IMPRINT",EDGE,{"derivedFrom":sQuery(id+"F2.wireOp",EDGE,"E12.1.0.1")}),-1.0]])]});
            var Q22;
            Q22=makeQuery(id+"F2.imprint","IMPRINT",FACE,{"disambiguationData":[TD([[makeQuery(id+"F2.imprint","IMPRINT",EDGE,{"derivedFrom":sQuery(id+"F2.wireOp",EDGE,"E11.2.0.2")}),-1.0]])]});
            var Q23;
            Q23=makeQuery(id+"F2.imprint","IMPRINT",FACE,{"disambiguationData":[TD([[makeQuery(id+"F2.imprint","IMPRINT",EDGE,{"derivedFrom":sQuery(id+"F2.wireOp",EDGE,"E8.2.0.1")}),-1.0]])]});
            var Q24;
            {var subQ0=sQuery(id+"F2.wireOp",EDGE,"E11.1.0.7");Q24=makeQuery(id+"F2.imprint","IMPRINT",FACE,{"disambiguationData":[TD([[makeQuery(id+"F2.imprint","IMPRINT",EDGE,{"derivedFrom":subQ0}),-1.0]])]});}
            var Q25;
            {var subQ1=sQuery(id+"F2.wireOp",EDGE,"E13.1.0.11");Q25=makeQuery(id+"F2.imprint","IMPRINT",FACE,{"disambiguationData":[TD([[makeQuery(id+"F2.imprint","IMPRINT",EDGE,{"derivedFrom":subQ1}),-1.0]])]});}
            var Q26;
            {var subQ0=sQuery(id+"F2.wireOp",EDGE,"E13.1.0.21");Q26=makeQuery(id+"F2.imprint","IMPRINT",FACE,{"disambiguationData":[TD([[makeQuery(id+"F2.imprint","IMPRINT",EDGE,{"derivedFrom":subQ0}),-1.0]])]});}
            var Q27;
            {var subQ4=sQuery(id+"F2.wireOp",EDGE,"E11.1.0.5");Q27=makeQuery(id+"F2.imprint","IMPRINT",FACE,{"disambiguationData":[TD([[makeQuery(id+"F2.imprint","IMPRINT",EDGE,{"derivedFrom":subQ4}),-1.0]])]});}
            var Q28;
            Q28=makeQuery(id+"F2.imprint","IMPRINT",FACE,{"disambiguationData":[TD([[makeQuery(id+"F2.imprint","IMPRINT",EDGE,{"derivedFrom":sQuery(id+"F2.wireOp",EDGE,"E8.1.0.1")}),-1.0]])]});
            var Q29;
            Q29=makeQuery(id+"F2.imprint","IMPRINT",FACE,{"disambiguationData":[TD([[makeQuery(id+"F2.imprint","IMPRINT",EDGE,{"derivedFrom":sQuery(id+"F2.wireOp",EDGE,"E7.0")}),-1.0]])]});
            var Q30;
            Q30=makeQuery(id+"F2.imprint","IMPRINT",FACE,{"disambiguationData":[TD([[makeQuery(id+"F2.imprint","IMPRINT",EDGE,{"derivedFrom":sQuery(id+"F2.wireOp",EDGE,"E12.1.0.12")}),-1.0]])]});
            var Q31;
            Q31=makeQuery(id+"F2.imprint","IMPRINT",FACE,{"disambiguationData":[TD([[makeQuery(id+"F2.imprint","IMPRINT",EDGE,{"derivedFrom":sQuery(id+"F2.wireOp",EDGE,"E13.1.0.1")}),-1.0]])]});
            var Q32;
            Q32=makeQuery(id+"F2.imprint","IMPRINT",FACE,{"disambiguationData":[TD([[makeQuery(id+"F2.imprint","IMPRINT",EDGE,{"derivedFrom":sQuery(id+"F2.wireOp",EDGE,"E10.0")}),-1.0]])]});
            var Q33;
            Q33=makeQuery(id+"F2.imprint","IMPRINT",FACE,{"disambiguationData":[TD([[makeQuery(id+"F2.imprint","IMPRINT",EDGE,{"derivedFrom":sQuery(id+"F2.wireOp",EDGE,"E41")}),1.0]])]});
            var Q34;
            Q34=makeQuery(id+"F2.imprint","IMPRINT",FACE,{"disambiguationData":[TD([[makeQuery(id+"F2.imprint","IMPRINT",EDGE,{"derivedFrom":sQuery(id+"F2.wireOp",EDGE,"E40")}),1.0]])]});
            var Q35;
            Q35=makeQuery(id+"F2.imprint","IMPRINT",FACE,{"disambiguationData":[TD([[makeQuery(id+"F2.imprint","IMPRINT",EDGE,{"derivedFrom":sQuery(id+"F2.wireOp",EDGE,"E52")}),1.0]])]});
            var Q36;
            Q36=makeQuery(id+"F2.imprint","IMPRINT",FACE,{"disambiguationData":[TD([[makeQuery(id+"F2.imprint","IMPRINT",EDGE,{"derivedFrom":sQuery(id+"F2.wireOp",EDGE,"E42")}),1.0]])]});
            var Q37;
            Q37=makeQuery(id+"F2.imprint","IMPRINT",FACE,{"disambiguationData":[TD([[makeQuery(id+"F2.imprint","IMPRINT",EDGE,{"derivedFrom":sQuery(id+"F2.wireOp",EDGE,"E43")}),1.0]])]});
            var Q38;
            Q38=makeQuery(id+"F2.imprint","IMPRINT",FACE,{"disambiguationData":[TD([[makeQuery(id+"F2.imprint","IMPRINT",EDGE,{"derivedFrom":sQuery(id+"F2.wireOp",EDGE,"E12.1.0.15")}),-1.0]])]});
            var Q39;
            Q39=makeQuery(id+"F2.imprint","IMPRINT",FACE,{"disambiguationData":[TD([[makeQuery(id+"F2.imprint","IMPRINT",EDGE,{"derivedFrom":sQuery(id+"F2.wireOp",EDGE,"E51")}),1.0]])]});
            var Q40;
            {var subQ0=sQuery(id+"F2.wireOp",EDGE,"E39");var subQ1=sQuery(id+"F2.wireOp",EDGE,"E13.1.0.22");var subQ2=makeQuery(id+"F2.imprint","INTERSECT",VERTEX,{"disambiguationData":[OD(0.0)],"derivedFrom":[subQ1,subQ0]});Q40=makeQuery(id+"F2.imprint","IMPRINT",FACE,{"disambiguationData":[TD([[makeQuery(id+"F2.imprint","IMPRINT",EDGE,{"disambiguationData":[TD([[subQ2,-1.0]])],"derivedFrom":subQ1}),1.0]])]});}
            var Q41;
            {var subQ0=sQuery(id+"F2.wireOp",EDGE,"E39");var subQ1=sQuery(id+"F2.wireOp",EDGE,"E13.1.0.22");var subQ2=makeQuery(id+"F2.imprint","INTERSECT",VERTEX,{"disambiguationData":[OD(0.0)],"derivedFrom":[subQ1,subQ0]});Q41=makeQuery(id+"F2.imprint","IMPRINT",FACE,{"disambiguationData":[TD([[makeQuery(id+"F2.imprint","IMPRINT",EDGE,{"disambiguationData":[TD([[subQ2,-1.0]])],"derivedFrom":subQ1}),-1.0]])]});}
            var Q42;
            {var subQ0=sQuery(id+"F2.wireOp",EDGE,"E38");var subQ1=sQuery(id+"F2.wireOp",EDGE,"E6.0.3");var subQ2=makeQuery(id+"F2.imprint","INTERSECT",VERTEX,{"disambiguationData":[OD(0.0)],"derivedFrom":[subQ1,subQ0]});Q42=makeQuery(id+"F2.imprint","IMPRINT",FACE,{"disambiguationData":[TD([[makeQuery(id+"F2.imprint","IMPRINT",EDGE,{"disambiguationData":[TD([[subQ2,-1.0]])],"derivedFrom":subQ1}),1.0]])]});}
            var Q43;
            {var subQ0=sQuery(id+"F2.wireOp",EDGE,"E38");var subQ1=sQuery(id+"F2.wireOp",EDGE,"E6.0.3");var subQ2=makeQuery(id+"F2.imprint","INTERSECT",VERTEX,{"disambiguationData":[OD(0.0)],"derivedFrom":[subQ1,subQ0]});Q43=makeQuery(id+"F2.imprint","IMPRINT",FACE,{"disambiguationData":[TD([[makeQuery(id+"F2.imprint","IMPRINT",EDGE,{"disambiguationData":[TD([[subQ2,-1.0]])],"derivedFrom":subQ1}),-1.0]])]});}
            var Q44;
            Q44=makeQuery(id+"F2.imprint","IMPRINT",FACE,{"disambiguationData":[TD([[makeQuery(id+"F2.imprint","IMPRINT",EDGE,{"derivedFrom":sQuery(id+"F2.wireOp",EDGE,"E50")}),1.0]])]});
            var Q45;
            Q45=makeQuery(id+"F2.imprint","IMPRINT",FACE,{"disambiguationData":[TD([[makeQuery(id+"F2.imprint","IMPRINT",EDGE,{"derivedFrom":sQuery(id+"F2.wireOp",EDGE,"E36")}),1.0]])]});
            var Q46;
            Q46=makeQuery(id+"F2.imprint","IMPRINT",FACE,{"disambiguationData":[TD([[makeQuery(id+"F2.imprint","IMPRINT",EDGE,{"derivedFrom":sQuery(id+"F2.wireOp",EDGE,"E13.1.0.24")}),-1.0]])]});
            var Q47;
            Q47=makeQuery(id+"F2.imprint","IMPRINT",FACE,{"disambiguationData":[TD([[makeQuery(id+"F2.imprint","IMPRINT",EDGE,{"derivedFrom":sQuery(id+"F2.wireOp",EDGE,"E47")}),1.0]])]});
            var Q48;
            Q48=makeQuery(id+"F2.imprint","IMPRINT",FACE,{"disambiguationData":[TD([[makeQuery(id+"F2.imprint","IMPRINT",EDGE,{"derivedFrom":sQuery(id+"F2.wireOp",EDGE,"E48")}),1.0]])]});
            var Q49;
            Q49=makeQuery(id+"F2.imprint","IMPRINT",FACE,{"disambiguationData":[TD([[makeQuery(id+"F2.imprint","IMPRINT",EDGE,{"derivedFrom":sQuery(id+"F2.wireOp",EDGE,"E49")}),1.0]])]});
            var Q50;
            Q50=makeQuery(id+"F2.imprint","IMPRINT",FACE,{"disambiguationData":[TD([[makeQuery(id+"F2.imprint","IMPRINT",EDGE,{"derivedFrom":sQuery(id+"F2.wireOp",EDGE,"E37")}),1.0]])]});
            var Q51;
            Q51=makeQuery(id+"F2.imprint","IMPRINT",FACE,{"disambiguationData":[TD([[makeQuery(id+"F2.imprint","IMPRINT",EDGE,{"derivedFrom":sQuery(id+"F2.wireOp",EDGE,"E53")}),1.0]])]});
            extrude(context, id + "F3", {"entities" : qUnion([Q0, Q1, Q2, Q3, Q4, Q5, Q6, Q7, Q8, Q9, Q10, Q11, Q12, Q13, Q14, Q15, Q16, Q17, Q18, Q19, Q20, Q21, Q22, Q23, Q24, Q25, Q26, Q27, Q28, Q29, Q30, Q31, Q32, Q33, Q34, Q35, Q36, Q37, Q38, Q39, Q40, Q41, Q42, Q43, Q44, Q45, Q46, Q47, Q48, Q49, Q50, Q51]), "operationType" : NewBodyOperationType.REMOVE, "oppositeDirection" : true, "depth" : 25 * mm, "offsetDistance" : 25 * mm});
        }
        {
            var Q0;
            Q0=makeQuery(id+"F1.opExtrude","CAP_EDGE",EDGE,{"disambiguationData":[OSD([sQuery(id+"F0.wireOp",EDGE,"E0.left")])],"isStart":true});
            var Q1;
            Q1=makeQuery(id+"F1.opExtrude","CAP_EDGE",EDGE,{"disambiguationData":[OSD([sQuery(id+"F0.wireOp",EDGE,"E2.right")])],"isStart":true});
            chamfer(context, id + "F4", {"entities" : qUnion([Q0, Q1]), "width" : 5 * mm, "tangentPropagation" : true});
        }
        {
            var Q0;
            Q0=makeQuery(id+"F1.opExtrude","CAP_EDGE",EDGE,{"disambiguationData":[OSD([sQuery(id+"F0.wireOp",EDGE,"E0.left")])],"isStart":false});
            var Q1;
            Q1=makeQuery(id+"F1.opExtrude","CAP_EDGE",EDGE,{"disambiguationData":[OSD([sQuery(id+"F0.wireOp",EDGE,"E2.right")])],"isStart":false});
            chamfer(context, id + "F5", {"entities" : qUnion([Q0, Q1]), "width" : 2.5 * mm, "tangentPropagation" : true});
        }
        {
            var Q0;
            {var subQ0=sQuery(id+"F0.wireOp",EDGE,"E1.left");var subQ1=sQuery(id+"F0.wireOp",EDGE,"E0.top");Q0=makeQuery(id+"F3.boolean.opBoolean","SPLIT",EDGE,{"disambiguationData":[TD([makeQuery(id+"F1.opExtrude","CAP_FACE",FACE,{"disambiguationData":[OSD([sQuery(id+"F0.wireOp",EDGE,"E0.bottom"),subQ1,sQuery(id+"F0.wireOp",EDGE,"E0.left"),sQuery(id+"F0.wireOp",EDGE,"E1.bottom"),sQuery(id+"F0.wireOp",EDGE,"E1.top"),subQ0,sQuery(id+"F0.wireOp",EDGE,"E2.bottom"),sQuery(id+"F0.wireOp",EDGE,"E2.top"),sQuery(id+"F0.wireOp",EDGE,"E2.left"),sQuery(id+"F0.wireOp",EDGE,"E2.right")])],"isStart":false})])],"derivedFrom":makeQuery(id+"F1.opExtrude","SWEPT_EDGE",EDGE,{"disambiguationData":[OSD([subQ1,subQ0])]})});}
            var Q1;
            {var subQ0=sQuery(id+"F0.wireOp",EDGE,"E0.top");var subQ1=sQuery(id+"F0.wireOp",EDGE,"E1.left");Q1=makeQuery(id+"F3.boolean.opBoolean","SPLIT",EDGE,{"disambiguationData":[TD([makeQuery(id+"F3.opExtrude","SWEPT_FACE",FACE,{"disambiguationData":[OSD([sQuery(id+"F2.wireOp",EDGE,"E11.3.0.6")])]})])],"derivedFrom":makeQuery(id+"F1.opExtrude","SWEPT_EDGE",EDGE,{"disambiguationData":[OSD([subQ0,subQ1])]})});}
            var Q2;
            {var subQ0=sQuery(id+"F0.wireOp",EDGE,"E0.top");var subQ1=sQuery(id+"F0.wireOp",EDGE,"E1.left");Q2=makeQuery(id+"F3.boolean.opBoolean","SPLIT",EDGE,{"disambiguationData":[TD([makeQuery(id+"F3.opExtrude","SWEPT_FACE",FACE,{"disambiguationData":[OSD([sQuery(id+"F2.wireOp",EDGE,"E13.1.0.40")])]})])],"derivedFrom":makeQuery(id+"F1.opExtrude","SWEPT_EDGE",EDGE,{"disambiguationData":[OSD([subQ0,subQ1])]})});}
            var Q3;
            {var subQ0=sQuery(id+"F0.wireOp",EDGE,"E1.left");var subQ1=sQuery(id+"F0.wireOp",EDGE,"E0.top");Q3=makeQuery(id+"F3.boolean.opBoolean","SPLIT",EDGE,{"disambiguationData":[TD([makeQuery(id+"F3.opExtrude","SWEPT_FACE",FACE,{"disambiguationData":[OSD([sQuery(id+"F2.wireOp",EDGE,"E13.1.0.41")])]})])],"derivedFrom":makeQuery(id+"F1.opExtrude","SWEPT_EDGE",EDGE,{"disambiguationData":[OSD([subQ1,subQ0])]})});}
            var Q4;
            {var subQ0=sQuery(id+"F0.wireOp",EDGE,"E0.top");var subQ1=sQuery(id+"F0.wireOp",EDGE,"E1.left");Q4=makeQuery(id+"F3.boolean.opBoolean","SPLIT",EDGE,{"disambiguationData":[TD([makeQuery(id+"F3.opExtrude","SWEPT_FACE",FACE,{"disambiguationData":[OSD([sQuery(id+"F2.wireOp",EDGE,"E11.3.0.2")])]})])],"derivedFrom":makeQuery(id+"F1.opExtrude","SWEPT_EDGE",EDGE,{"disambiguationData":[OSD([subQ0,subQ1])]})});}
            fillet(context, id + "F6", {"entities" : qUnion([Q0, Q1, Q2, Q3, Q4]), "radius" : 1 * mm, "tangentPropagation" : true, "allowEdgeOverflow" : false});
        }
        {
            var Q0;
            {var subQ0=sQuery(id+"F0.wireOp",EDGE,"E2.left");var subQ1=sQuery(id+"F0.wireOp",EDGE,"E1.top");Q0=makeQuery(id+"F3.boolean.opBoolean","SPLIT",EDGE,{"disambiguationData":[TD([makeQuery(id+"F1.opExtrude","CAP_FACE",FACE,{"disambiguationData":[OSD([sQuery(id+"F0.wireOp",EDGE,"E0.bottom"),sQuery(id+"F0.wireOp",EDGE,"E0.top"),sQuery(id+"F0.wireOp",EDGE,"E0.left"),sQuery(id+"F0.wireOp",EDGE,"E1.bottom"),subQ1,sQuery(id+"F0.wireOp",EDGE,"E1.left"),sQuery(id+"F0.wireOp",EDGE,"E2.bottom"),sQuery(id+"F0.wireOp",EDGE,"E2.top"),subQ0,sQuery(id+"F0.wireOp",EDGE,"E2.right")])],"isStart":false})])],"derivedFrom":makeQuery(id+"F1.opExtrude","SWEPT_EDGE",EDGE,{"disambiguationData":[OSD([subQ1,subQ0])]})});}
            var Q1;
            {var subQ0=sQuery(id+"F0.wireOp",EDGE,"E2.left");var subQ1=sQuery(id+"F0.wireOp",EDGE,"E1.top");Q1=makeQuery(id+"F3.boolean.opBoolean","SPLIT",EDGE,{"disambiguationData":[TD([makeQuery(id+"F3.opExtrude","SWEPT_FACE",FACE,{"disambiguationData":[OSD([sQuery(id+"F2.wireOp",EDGE,"E13.1.0.16")])]})])],"derivedFrom":makeQuery(id+"F1.opExtrude","SWEPT_EDGE",EDGE,{"disambiguationData":[OSD([subQ1,subQ0])]})});}
            var Q2;
            {var subQ0=sQuery(id+"F0.wireOp",EDGE,"E1.top");var subQ1=sQuery(id+"F0.wireOp",EDGE,"E2.left");Q2=makeQuery(id+"F3.boolean.opBoolean","SPLIT",EDGE,{"disambiguationData":[TD([makeQuery(id+"F3.opExtrude","SWEPT_FACE",FACE,{"disambiguationData":[OSD([sQuery(id+"F2.wireOp",EDGE,"E13.1.0.13")])]})])],"derivedFrom":makeQuery(id+"F1.opExtrude","SWEPT_EDGE",EDGE,{"disambiguationData":[OSD([subQ0,subQ1])]})});}
            var Q3;
            {var subQ0=sQuery(id+"F0.wireOp",EDGE,"E1.top");var subQ1=sQuery(id+"F0.wireOp",EDGE,"E2.left");Q3=makeQuery(id+"F3.boolean.opBoolean","SPLIT",EDGE,{"disambiguationData":[TD([makeQuery(id+"F3.opExtrude","SWEPT_FACE",FACE,{"disambiguationData":[OSD([sQuery(id+"F2.wireOp",EDGE,"E11.1.0.6")])]})])],"derivedFrom":makeQuery(id+"F1.opExtrude","SWEPT_EDGE",EDGE,{"disambiguationData":[OSD([subQ0,subQ1])]})});}
            var Q4;
            {var subQ0=sQuery(id+"F0.wireOp",EDGE,"E1.top");var subQ1=sQuery(id+"F0.wireOp",EDGE,"E2.left");Q4=makeQuery(id+"F3.boolean.opBoolean","SPLIT",EDGE,{"disambiguationData":[TD([makeQuery(id+"F3.opExtrude","SWEPT_FACE",FACE,{"disambiguationData":[OSD([sQuery(id+"F2.wireOp",EDGE,"E11.1.0.2")])]})])],"derivedFrom":makeQuery(id+"F1.opExtrude","SWEPT_EDGE",EDGE,{"disambiguationData":[OSD([subQ0,subQ1])]})});}
            fillet(context, id + "F7", {"entities" : qUnion([Q0, Q1, Q2, Q3, Q4]), "radius" : 1 * mm, "tangentPropagation" : true, "allowEdgeOverflow" : false});
        }
        {
            var Q0;
            {var subQ0=sQuery(id+"F0.wireOp",EDGE,"E2.top");var subQ1=sQuery(id+"F0.wireOp",EDGE,"E2.left");var subQ2=sQuery(id+"F0.wireOp",EDGE,"E1.top");Q0=makeQuery(id+"F7.opFillet","BLEND_EDGE",EDGE,{"blendedFrom":[makeQuery(id+"F3.boolean.opBoolean","SPLIT",EDGE,{"disambiguationData":[TD([makeQuery(id+"F3.opExtrude","SWEPT_FACE",FACE,{"disambiguationData":[OSD([sQuery(id+"F2.wireOp",EDGE,"E13.1.0.16")])]})])],"derivedFrom":makeQuery(id+"F1.opExtrude","SWEPT_EDGE",EDGE,{"disambiguationData":[OSD([subQ2,subQ1])]})}),makeQuery(id+"F1.opExtrude","SWEPT_FACE",FACE,{"disambiguationData":[OSD([subQ0])]})],"blendedInto":[makeQuery(id+"F1.opExtrude","SWEPT_FACE",FACE,{"disambiguationData":[OSD([subQ0])]})]});}
            var Q1;
            {var subQ0=sQuery(id+"F0.wireOp",EDGE,"E1.top");var subQ1=sQuery(id+"F0.wireOp",EDGE,"E2.left");Q1=makeQuery(id+"F7.opFillet","BLEND_EDGE",EDGE,{"blendedFrom":[makeQuery(id+"F3.boolean.opBoolean","SPLIT",EDGE,{"disambiguationData":[TD([makeQuery(id+"F3.opExtrude","SWEPT_FACE",FACE,{"disambiguationData":[OSD([sQuery(id+"F2.wireOp",EDGE,"E13.1.0.13")])]})])],"derivedFrom":makeQuery(id+"F1.opExtrude","SWEPT_EDGE",EDGE,{"disambiguationData":[OSD([subQ0,subQ1])]})}),makeQuery(id+"F1.opExtrude","SWEPT_FACE",FACE,{"disambiguationData":[OSD([sQuery(id+"F0.wireOp",EDGE,"E2.top")])]})],"blendedInto":[makeQuery(id+"F1.opExtrude","SWEPT_FACE",FACE,{"disambiguationData":[OSD([sQuery(id+"F0.wireOp",EDGE,"E2.top")])]})]});}
            var Q2;
            {var subQ0=sQuery(id+"F0.wireOp",EDGE,"E1.top");var subQ1=sQuery(id+"F0.wireOp",EDGE,"E2.left");Q2=makeQuery(id+"F7.opFillet","BLEND_EDGE",EDGE,{"blendedFrom":[makeQuery(id+"F3.boolean.opBoolean","SPLIT",EDGE,{"disambiguationData":[TD([makeQuery(id+"F3.opExtrude","SWEPT_FACE",FACE,{"disambiguationData":[OSD([sQuery(id+"F2.wireOp",EDGE,"E11.1.0.6")])]})])],"derivedFrom":makeQuery(id+"F1.opExtrude","SWEPT_EDGE",EDGE,{"disambiguationData":[OSD([subQ0,subQ1])]})}),makeQuery(id+"F1.opExtrude","SWEPT_FACE",FACE,{"disambiguationData":[OSD([sQuery(id+"F0.wireOp",EDGE,"E2.top")])]})],"blendedInto":[makeQuery(id+"F1.opExtrude","SWEPT_FACE",FACE,{"disambiguationData":[OSD([sQuery(id+"F0.wireOp",EDGE,"E2.top")])]})]});}
            var Q3;
            {var subQ0=sQuery(id+"F0.wireOp",EDGE,"E1.top");var subQ1=sQuery(id+"F0.wireOp",EDGE,"E2.left");Q3=makeQuery(id+"F7.opFillet","BLEND_EDGE",EDGE,{"blendedFrom":[makeQuery(id+"F3.boolean.opBoolean","SPLIT",EDGE,{"disambiguationData":[TD([makeQuery(id+"F3.opExtrude","SWEPT_FACE",FACE,{"disambiguationData":[OSD([sQuery(id+"F2.wireOp",EDGE,"E11.1.0.2")])]})])],"derivedFrom":makeQuery(id+"F1.opExtrude","SWEPT_EDGE",EDGE,{"disambiguationData":[OSD([subQ0,subQ1])]})}),makeQuery(id+"F1.opExtrude","SWEPT_FACE",FACE,{"disambiguationData":[OSD([sQuery(id+"F0.wireOp",EDGE,"E2.top")])]})],"blendedInto":[makeQuery(id+"F1.opExtrude","SWEPT_FACE",FACE,{"disambiguationData":[OSD([sQuery(id+"F0.wireOp",EDGE,"E2.top")])]})]});}
            var Q4;
            {var subQ0=sQuery(id+"F0.wireOp",EDGE,"E2.top");var subQ1=sQuery(id+"F0.wireOp",EDGE,"E2.left");var subQ2=sQuery(id+"F0.wireOp",EDGE,"E1.top");Q4=makeQuery(id+"F7.opFillet","BLEND_EDGE",EDGE,{"blendedFrom":[makeQuery(id+"F3.boolean.opBoolean","SPLIT",EDGE,{"disambiguationData":[TD([makeQuery(id+"F1.opExtrude","CAP_FACE",FACE,{"disambiguationData":[OSD([sQuery(id+"F0.wireOp",EDGE,"E0.bottom"),sQuery(id+"F0.wireOp",EDGE,"E0.top"),sQuery(id+"F0.wireOp",EDGE,"E0.left"),sQuery(id+"F0.wireOp",EDGE,"E1.bottom"),subQ2,sQuery(id+"F0.wireOp",EDGE,"E1.left"),sQuery(id+"F0.wireOp",EDGE,"E2.bottom"),subQ0,subQ1,sQuery(id+"F0.wireOp",EDGE,"E2.right")])],"isStart":false})])],"derivedFrom":makeQuery(id+"F1.opExtrude","SWEPT_EDGE",EDGE,{"disambiguationData":[OSD([subQ2,subQ1])]})}),makeQuery(id+"F1.opExtrude","SWEPT_FACE",FACE,{"disambiguationData":[OSD([subQ0])]})],"blendedInto":[makeQuery(id+"F1.opExtrude","SWEPT_FACE",FACE,{"disambiguationData":[OSD([subQ0])]})]});}
            var Q5;
            {var subQ0=sQuery(id+"F0.wireOp",EDGE,"E1.top");var subQ1=sQuery(id+"F0.wireOp",EDGE,"E1.left");var subQ2=sQuery(id+"F0.wireOp",EDGE,"E0.top");Q5=makeQuery(id+"F6.opFillet","BLEND_EDGE",EDGE,{"blendedFrom":[makeQuery(id+"F3.boolean.opBoolean","SPLIT",EDGE,{"disambiguationData":[TD([makeQuery(id+"F1.opExtrude","CAP_FACE",FACE,{"disambiguationData":[OSD([sQuery(id+"F0.wireOp",EDGE,"E0.bottom"),subQ2,sQuery(id+"F0.wireOp",EDGE,"E0.left"),sQuery(id+"F0.wireOp",EDGE,"E1.bottom"),subQ0,subQ1,sQuery(id+"F0.wireOp",EDGE,"E2.bottom"),sQuery(id+"F0.wireOp",EDGE,"E2.top"),sQuery(id+"F0.wireOp",EDGE,"E2.left"),sQuery(id+"F0.wireOp",EDGE,"E2.right")])],"isStart":false})])],"derivedFrom":makeQuery(id+"F1.opExtrude","SWEPT_EDGE",EDGE,{"disambiguationData":[OSD([subQ2,subQ1])]})}),makeQuery(id+"F1.opExtrude","SWEPT_FACE",FACE,{"disambiguationData":[OSD([subQ0])]})],"blendedInto":[makeQuery(id+"F1.opExtrude","SWEPT_FACE",FACE,{"disambiguationData":[OSD([subQ0])]})]});}
            var Q6;
            {var subQ0=sQuery(id+"F0.wireOp",EDGE,"E0.top");var subQ1=sQuery(id+"F0.wireOp",EDGE,"E1.left");Q6=makeQuery(id+"F6.opFillet","BLEND_EDGE",EDGE,{"blendedFrom":[makeQuery(id+"F3.boolean.opBoolean","SPLIT",EDGE,{"disambiguationData":[TD([makeQuery(id+"F3.opExtrude","SWEPT_FACE",FACE,{"disambiguationData":[OSD([sQuery(id+"F2.wireOp",EDGE,"E11.3.0.2")])]})])],"derivedFrom":makeQuery(id+"F1.opExtrude","SWEPT_EDGE",EDGE,{"disambiguationData":[OSD([subQ0,subQ1])]})}),makeQuery(id+"F1.opExtrude","SWEPT_FACE",FACE,{"disambiguationData":[OSD([sQuery(id+"F0.wireOp",EDGE,"E1.top")])]})],"blendedInto":[makeQuery(id+"F1.opExtrude","SWEPT_FACE",FACE,{"disambiguationData":[OSD([sQuery(id+"F0.wireOp",EDGE,"E1.top")])]})]});}
            var Q7;
            {var subQ0=sQuery(id+"F0.wireOp",EDGE,"E0.top");var subQ1=sQuery(id+"F0.wireOp",EDGE,"E1.left");Q7=makeQuery(id+"F6.opFillet","BLEND_EDGE",EDGE,{"blendedFrom":[makeQuery(id+"F3.boolean.opBoolean","SPLIT",EDGE,{"disambiguationData":[TD([makeQuery(id+"F3.opExtrude","SWEPT_FACE",FACE,{"disambiguationData":[OSD([sQuery(id+"F2.wireOp",EDGE,"E11.3.0.6")])]})])],"derivedFrom":makeQuery(id+"F1.opExtrude","SWEPT_EDGE",EDGE,{"disambiguationData":[OSD([subQ0,subQ1])]})}),makeQuery(id+"F1.opExtrude","SWEPT_FACE",FACE,{"disambiguationData":[OSD([sQuery(id+"F0.wireOp",EDGE,"E1.top")])]})],"blendedInto":[makeQuery(id+"F1.opExtrude","SWEPT_FACE",FACE,{"disambiguationData":[OSD([sQuery(id+"F0.wireOp",EDGE,"E1.top")])]})]});}
            var Q8;
            {var subQ0=sQuery(id+"F0.wireOp",EDGE,"E0.top");var subQ1=sQuery(id+"F0.wireOp",EDGE,"E1.left");Q8=makeQuery(id+"F6.opFillet","BLEND_EDGE",EDGE,{"blendedFrom":[makeQuery(id+"F3.boolean.opBoolean","SPLIT",EDGE,{"disambiguationData":[TD([makeQuery(id+"F3.opExtrude","SWEPT_FACE",FACE,{"disambiguationData":[OSD([sQuery(id+"F2.wireOp",EDGE,"E13.1.0.40")])]})])],"derivedFrom":makeQuery(id+"F1.opExtrude","SWEPT_EDGE",EDGE,{"disambiguationData":[OSD([subQ0,subQ1])]})}),makeQuery(id+"F1.opExtrude","SWEPT_FACE",FACE,{"disambiguationData":[OSD([sQuery(id+"F0.wireOp",EDGE,"E1.top")])]})],"blendedInto":[makeQuery(id+"F1.opExtrude","SWEPT_FACE",FACE,{"disambiguationData":[OSD([sQuery(id+"F0.wireOp",EDGE,"E1.top")])]})]});}
            var Q9;
            {var subQ0=sQuery(id+"F0.wireOp",EDGE,"E1.top");var subQ1=sQuery(id+"F0.wireOp",EDGE,"E1.left");var subQ2=sQuery(id+"F0.wireOp",EDGE,"E0.top");Q9=makeQuery(id+"F6.opFillet","BLEND_EDGE",EDGE,{"blendedFrom":[makeQuery(id+"F3.boolean.opBoolean","SPLIT",EDGE,{"disambiguationData":[TD([makeQuery(id+"F3.opExtrude","SWEPT_FACE",FACE,{"disambiguationData":[OSD([sQuery(id+"F2.wireOp",EDGE,"E13.1.0.41")])]})])],"derivedFrom":makeQuery(id+"F1.opExtrude","SWEPT_EDGE",EDGE,{"disambiguationData":[OSD([subQ2,subQ1])]})}),makeQuery(id+"F1.opExtrude","SWEPT_FACE",FACE,{"disambiguationData":[OSD([subQ0])]})],"blendedInto":[makeQuery(id+"F1.opExtrude","SWEPT_FACE",FACE,{"disambiguationData":[OSD([subQ0])]})]});}
            fillet(context, id + "F8", {"entities" : qUnion([Q0, Q1, Q2, Q3, Q4, Q5, Q6, Q7, Q8, Q9]), "radius" : 1 * mm, "tangentPropagation" : true, "allowEdgeOverflow" : false});
        }
        {
            var Q0;
            {var subQ0=sQuery(id+"F0.wireOp",EDGE,"E2.right");Q0=makeQuery(id+"F4.opChamfer","BLEND_EDGE",EDGE,{"blendedFrom":[makeQuery(id+"F1.opExtrude","CAP_EDGE",EDGE,{"disambiguationData":[OSD([subQ0])],"isStart":true}),makeQuery(id+"F1.opExtrude","SWEPT_FACE",FACE,{"disambiguationData":[OSD([subQ0])]})],"blendedInto":[makeQuery(id+"F1.opExtrude","SWEPT_FACE",FACE,{"disambiguationData":[OSD([subQ0])]})]});}
            var Q1;
            {var subQ0=sQuery(id+"F0.wireOp",EDGE,"E2.right");Q1=makeQuery(id+"F5.opChamfer","BLEND_EDGE",EDGE,{"blendedFrom":[makeQuery(id+"F1.opExtrude","CAP_EDGE",EDGE,{"disambiguationData":[OSD([subQ0])],"isStart":false}),makeQuery(id+"F1.opExtrude","SWEPT_FACE",FACE,{"disambiguationData":[OSD([subQ0])]})],"blendedInto":[makeQuery(id+"F1.opExtrude","SWEPT_FACE",FACE,{"disambiguationData":[OSD([subQ0])]})]});}
            var Q2;
            {var subQ0=sQuery(id+"F0.wireOp",EDGE,"E2.right");Q2=makeQuery(id+"F5.opChamfer","BLEND_EDGE",EDGE,{"blendedFrom":[makeQuery(id+"F1.opExtrude","CAP_EDGE",EDGE,{"disambiguationData":[OSD([subQ0])],"isStart":false}),makeQuery(id+"F1.opExtrude","CAP_FACE",FACE,{"disambiguationData":[OSD([sQuery(id+"F0.wireOp",EDGE,"E0.bottom"),sQuery(id+"F0.wireOp",EDGE,"E0.top"),sQuery(id+"F0.wireOp",EDGE,"E0.left"),sQuery(id+"F0.wireOp",EDGE,"E1.bottom"),sQuery(id+"F0.wireOp",EDGE,"E1.top"),sQuery(id+"F0.wireOp",EDGE,"E1.left"),sQuery(id+"F0.wireOp",EDGE,"E2.bottom"),sQuery(id+"F0.wireOp",EDGE,"E2.top"),sQuery(id+"F0.wireOp",EDGE,"E2.left"),subQ0])],"isStart":false})],"blendedInto":[makeQuery(id+"F1.opExtrude","CAP_FACE",FACE,{"disambiguationData":[OSD([sQuery(id+"F0.wireOp",EDGE,"E0.bottom"),sQuery(id+"F0.wireOp",EDGE,"E0.top"),sQuery(id+"F0.wireOp",EDGE,"E0.left"),sQuery(id+"F0.wireOp",EDGE,"E1.bottom"),sQuery(id+"F0.wireOp",EDGE,"E1.top"),sQuery(id+"F0.wireOp",EDGE,"E1.left"),sQuery(id+"F0.wireOp",EDGE,"E2.bottom"),sQuery(id+"F0.wireOp",EDGE,"E2.top"),sQuery(id+"F0.wireOp",EDGE,"E2.left"),subQ0])],"isStart":false})]});}
            var Q3;
            {var subQ0=sQuery(id+"F0.wireOp",EDGE,"E0.left");Q3=makeQuery(id+"F5.opChamfer","BLEND_EDGE",EDGE,{"blendedFrom":[makeQuery(id+"F1.opExtrude","CAP_EDGE",EDGE,{"disambiguationData":[OSD([subQ0])],"isStart":false}),makeQuery(id+"F1.opExtrude","CAP_FACE",FACE,{"disambiguationData":[OSD([sQuery(id+"F0.wireOp",EDGE,"E0.bottom"),sQuery(id+"F0.wireOp",EDGE,"E0.top"),subQ0,sQuery(id+"F0.wireOp",EDGE,"E1.bottom"),sQuery(id+"F0.wireOp",EDGE,"E1.top"),sQuery(id+"F0.wireOp",EDGE,"E1.left"),sQuery(id+"F0.wireOp",EDGE,"E2.bottom"),sQuery(id+"F0.wireOp",EDGE,"E2.top"),sQuery(id+"F0.wireOp",EDGE,"E2.left"),sQuery(id+"F0.wireOp",EDGE,"E2.right")])],"isStart":false})],"blendedInto":[makeQuery(id+"F1.opExtrude","CAP_FACE",FACE,{"disambiguationData":[OSD([sQuery(id+"F0.wireOp",EDGE,"E0.bottom"),sQuery(id+"F0.wireOp",EDGE,"E0.top"),subQ0,sQuery(id+"F0.wireOp",EDGE,"E1.bottom"),sQuery(id+"F0.wireOp",EDGE,"E1.top"),sQuery(id+"F0.wireOp",EDGE,"E1.left"),sQuery(id+"F0.wireOp",EDGE,"E2.bottom"),sQuery(id+"F0.wireOp",EDGE,"E2.top"),sQuery(id+"F0.wireOp",EDGE,"E2.left"),sQuery(id+"F0.wireOp",EDGE,"E2.right")])],"isStart":false})]});}
            var Q4;
            {var subQ0=sQuery(id+"F0.wireOp",EDGE,"E0.left");Q4=makeQuery(id+"F5.opChamfer","BLEND_EDGE",EDGE,{"blendedFrom":[makeQuery(id+"F1.opExtrude","CAP_EDGE",EDGE,{"disambiguationData":[OSD([subQ0])],"isStart":false}),makeQuery(id+"F1.opExtrude","SWEPT_FACE",FACE,{"disambiguationData":[OSD([subQ0])]})],"blendedInto":[makeQuery(id+"F1.opExtrude","SWEPT_FACE",FACE,{"disambiguationData":[OSD([subQ0])]})]});}
            var Q5;
            {var subQ0=sQuery(id+"F0.wireOp",EDGE,"E0.left");Q5=makeQuery(id+"F4.opChamfer","BLEND_EDGE",EDGE,{"blendedFrom":[makeQuery(id+"F1.opExtrude","CAP_EDGE",EDGE,{"disambiguationData":[OSD([subQ0])],"isStart":true}),makeQuery(id+"F1.opExtrude","SWEPT_FACE",FACE,{"disambiguationData":[OSD([subQ0])]})],"blendedInto":[makeQuery(id+"F1.opExtrude","SWEPT_FACE",FACE,{"disambiguationData":[OSD([subQ0])]})]});}
            fillet(context, id + "F9", {"entities" : qUnion([Q0, Q1, Q2, Q3, Q4, Q5]), "radius" : 5 * mm, "tangentPropagation" : true, "allowEdgeOverflow" : false});
        }
    });
